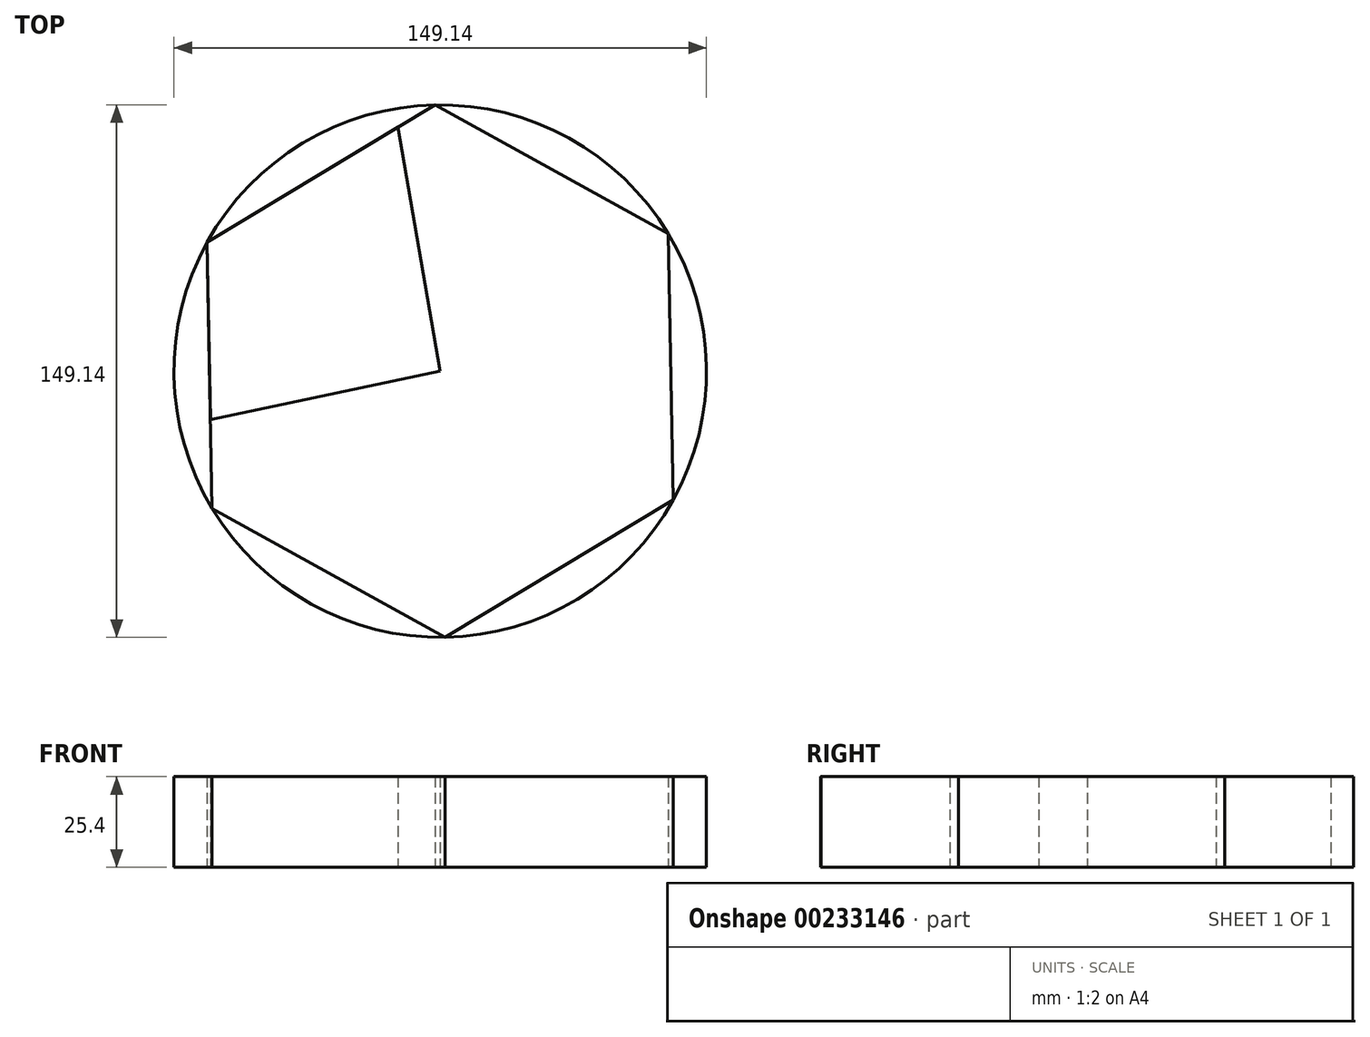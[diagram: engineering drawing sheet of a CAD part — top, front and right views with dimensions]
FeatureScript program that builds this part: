
annotation { "Feature Type Name" : "Feature", "Feature Type Description" : "" }
export const myFeature = defineFeature(function(context is Context, id is Id, definition is map)
    precondition{}
    {
        {
            var Q0;
            Q0=qCreatedBy(makeId("Top.planeOp"),FACE);
            var sketch = newSketch(context, id + "F0", { "sketchPlane" : qUnion([Q0])});
            skCircle(sketch, "E0", {"center": v(0, 0) * mm, "radius": 74.57 * mm});
            skLineSegment(sketch, "E1.0", {"start": v(-1.4, 74.55) * mm, "end": v(63.86, 38.5) * mm});
            skLineSegment(sketch, "E1.1", {"start": v(63.86, 38.5) * mm, "end": v(65.27, -36.06) * mm});
            skLineSegment(sketch, "E1.2", {"start": v(65.27, -36.06) * mm, "end": v(1.4, -74.55) * mm});
            skLineSegment(sketch, "E1.3", {"start": v(1.4, -74.55) * mm, "end": v(-63.86, -38.5) * mm});
            skLineSegment(sketch, "E1.4", {"start": v(-63.86, -38.5) * mm, "end": v(-65.27, 36.06) * mm});
            skLineSegment(sketch, "E1.5", {"start": v(-65.27, 36.06) * mm, "end": v(-1.4, 74.55) * mm});
            skPoint(sketch, "E1.0.midPoint", {"position": v(31.23, 56.52) * mm});
            skLineSegment(sketch, "E2", {"start": v(0, 0) * mm, "end": v(38.27, 52.01) * mm});
            skLineSegment(sketch, "E3", {"start": v(0, 0) * mm, "end": v(19.92, 62.77) * mm});
            skLineSegment(sketch, "E4", {"start": v(0, 0) * mm, "end": v(-11.83, 68.27) * mm});
            skLineSegment(sketch, "E5", {"start": v(0, 0) * mm, "end": v(-33.34, 55.3) * mm});
            skPoint(sketch, "E5.endSnap0", {"position": v(-33.34, 55.3) * mm});
            skLineSegment(sketch, "E6", {"start": v(0, 0) * mm, "end": v(-52.75, 43.6) * mm});
            skLineSegment(sketch, "E7", {"start": v(0, 0) * mm, "end": v(-65.03, 23.5) * mm});
            skLineSegment(sketch, "E8", {"start": v(0, 0) * mm, "end": v(63.86, 38.5) * mm});
            skLineSegment(sketch, "E9", {"start": v(0, 0) * mm, "end": v(63.63, 11.03) * mm});
            skLineSegment(sketch, "E10", {"start": v(0, 0) * mm, "end": v(-64.32, 5.77) * mm});
            skLineSegment(sketch, "E11.MirrorCS", {"start": v(0, 0) * mm, "end": v(-45.03, 36.9) * mm});
            skLineSegment(sketch, "E12", {"start": v(0, 0) * mm, "end": v(-64.33, -13.59) * mm});
            skLineSegment(sketch, "E13", {"start": v(0, 0) * mm, "end": v(-56.83, -42.38) * mm});
            skLineSegment(sketch, "E14", {"start": v(0, 0) * mm, "end": v(-28.74, -57.9) * mm});
            skLineSegment(sketch, "E15", {"start": v(0, 0) * mm, "end": v(3.97, -73) * mm});
            skLineSegment(sketch, "E16", {"start": v(0, 0) * mm, "end": v(29.18, -57.6) * mm});
            skLineSegment(sketch, "E17", {"start": v(0, 0) * mm, "end": v(52.2, -43.94) * mm});
            skLineSegment(sketch, "E18", {"start": v(0, 0) * mm, "end": v(64.92, -17.53) * mm});
            skArc(sketch, "E19.trimOffspring", {"start": v(38.27, 52.01) * mm, "mid": v(34.82, 54.38) * mm, "end": v(31.23, 56.52) * mm, "construction": true});
            skArc(sketch, "E20.trimOffspring", {"start": v(29.18, -57.6) * mm, "mid": v(31.28, -56.5) * mm, "end": v(33.34, -55.3) * mm, "construction": true});
            skArc(sketch, "E21.trimOffspring", {"start": v(-31.23, -56.52) * mm, "mid": v(-29.99, -57.23) * mm, "end": v(-28.74, -57.9) * mm, "construction": true});
            skSolve(sketch);
        }
        {
            var Q0;
            {var subQ0=sQuery(id+"F0.wireOp",EDGE,"E1.1");var subQ4=makeQuery(id+"F0.imprint","INTERSECT",VERTEX,{"derivedFrom":[subQ0,sQuery(id+"F0.wireOp",EDGE,"E18")]});Q0=makeQuery(id+"F0.imprint","IMPRINT",FACE,{"disambiguationData":[TD([[makeQuery(id+"F0.imprint","IMPRINT",EDGE,{"disambiguationData":[TD([[subQ4,-1.0]])],"derivedFrom":subQ0}),1.0]])]});}
            var Q1;
            {var subQ0=sQuery(id+"F0.wireOp",EDGE,"E1.0");var subQ4=makeQuery(id+"F0.imprint","INTERSECT",VERTEX,{"derivedFrom":[subQ0,sQuery(id+"F0.wireOp",EDGE,"E3")]});Q1=makeQuery(id+"F0.imprint","IMPRINT",FACE,{"disambiguationData":[TD([[makeQuery(id+"F0.imprint","IMPRINT",EDGE,{"disambiguationData":[TD([[subQ4,1.0]])],"derivedFrom":subQ0}),1.0]])]});}
            var Q2;
            {var subQ0=sQuery(id+"F0.wireOp",EDGE,"E1.5");var subQ2=makeQuery(id+"F0.imprint","INTERSECT",VERTEX,{"derivedFrom":[subQ0,sQuery(id+"F0.wireOp",EDGE,"E5")]});Q2=makeQuery(id+"F0.imprint","IMPRINT",FACE,{"disambiguationData":[TD([[makeQuery(id+"F0.imprint","IMPRINT",EDGE,{"disambiguationData":[TD([[subQ2,1.0]])],"derivedFrom":subQ0}),1.0]])]});}
            var Q3;
            {var subQ0=sQuery(id+"F0.wireOp",EDGE,"E1.3");var subQ5=makeQuery(id+"F0.imprint","INTERSECT",VERTEX,{"derivedFrom":[subQ0,sQuery(id+"F0.wireOp",EDGE,"E13")]});Q3=makeQuery(id+"F0.imprint","IMPRINT",FACE,{"disambiguationData":[TD([[makeQuery(id+"F0.imprint","IMPRINT",EDGE,{"disambiguationData":[TD([[subQ5,1.0]])],"derivedFrom":subQ0}),1.0]])]});}
            var Q4;
            {var subQ0=sQuery(id+"F0.wireOp",EDGE,"E1.2");var subQ5=makeQuery(id+"F0.imprint","INTERSECT",VERTEX,{"derivedFrom":[subQ0,sQuery(id+"F0.wireOp",EDGE,"E15")]});Q4=makeQuery(id+"F0.imprint","IMPRINT",FACE,{"disambiguationData":[TD([[makeQuery(id+"F0.imprint","IMPRINT",EDGE,{"disambiguationData":[TD([[subQ5,1.0]])],"derivedFrom":subQ0}),1.0]])]});}
            var Q5;
            {var subQ0=sQuery(id+"F0.wireOp",EDGE,"E1.4");var subQ5=makeQuery(id+"F0.imprint","INTERSECT",VERTEX,{"derivedFrom":[subQ0,sQuery(id+"F0.wireOp",EDGE,"E7")]});Q5=makeQuery(id+"F0.imprint","IMPRINT",FACE,{"disambiguationData":[TD([[makeQuery(id+"F0.imprint","IMPRINT",EDGE,{"disambiguationData":[TD([[subQ5,1.0]])],"derivedFrom":subQ0}),1.0]])]});}
            extrude(context, id + "F1", {"entities" : qUnion([Q0, Q1, Q2, Q3, Q4, Q5]), "depth" : 25.4 * mm});
        }
        {
            var Q0;
            {var subQ0=sQuery(id+"F0.wireOp",EDGE,"E4");Q0=makeQuery(id+"F0.imprint","IMPRINT",FACE,{"disambiguationData":[TD([[makeQuery(id+"F0.imprint","IMPRINT",EDGE,{"derivedFrom":subQ0}),1.0]])]});}
            var Q1;
            {var subQ0=sQuery(id+"F0.wireOp",EDGE,"E5");Q1=makeQuery(id+"F0.imprint","IMPRINT",FACE,{"disambiguationData":[TD([[makeQuery(id+"F0.imprint","IMPRINT",EDGE,{"derivedFrom":subQ0}),1.0]])]});}
            var Q2;
            {var subQ4=sQuery(id+"F0.wireOp",EDGE,"E6");Q2=makeQuery(id+"F0.imprint","IMPRINT",FACE,{"disambiguationData":[TD([[makeQuery(id+"F0.imprint","IMPRINT",EDGE,{"derivedFrom":subQ4}),1.0]])]});}
            var Q3;
            {var subQ0=sQuery(id+"F0.wireOp",EDGE,"E7");Q3=makeQuery(id+"F0.imprint","IMPRINT",FACE,{"disambiguationData":[TD([[makeQuery(id+"F0.imprint","IMPRINT",EDGE,{"derivedFrom":subQ0}),1.0]])]});}
            extrude(context, id + "F2", {"entities" : qUnion([Q0, Q1, Q2, Q3]), "depth" : 25.4 * mm});
        }
    });
